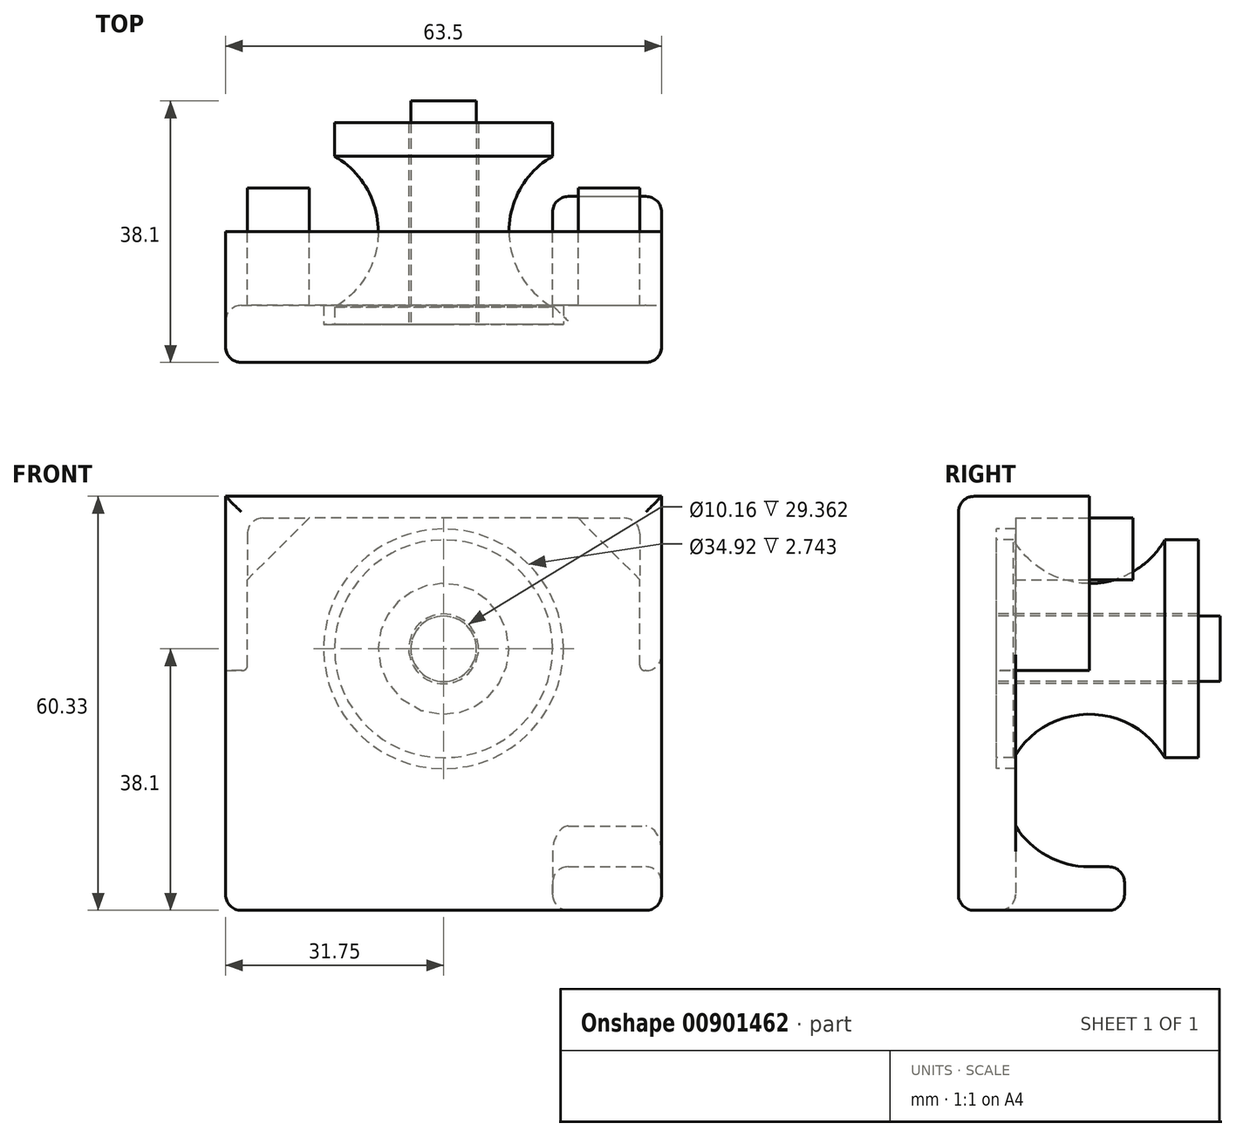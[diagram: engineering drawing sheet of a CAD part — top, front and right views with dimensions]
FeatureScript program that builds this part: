
annotation { "Feature Type Name" : "Feature", "Feature Type Description" : "" }
export const myFeature = defineFeature(function(context is Context, id is Id, definition is map)
    precondition{}
    {
        {
            var Q0;
            Q0=qCreatedBy(makeId("Right.planeOp"),FACE);
            var sketch = newSketch(context, id + "F0", { "sketchPlane" : qUnion([Q0])});
            skLineSegment(sketch, "E0", {"start": v(-15.88, 0) * mm, "end": v(15.88, 0) * mm});
            skLineSegment(sketch, "E1", {"start": v(-15.88, 0) * mm, "end": v(-15.88, 15.88) * mm});
            skArc(sketch, "E2", {"start": v(-11, 15.88) * mm, "mid": v(-6.35, 11.23) * mm, "end": v(0, 9.53) * mm});
            skLineSegment(sketch, "E3", {"start": v(-15.88, 15.88) * mm, "end": v(-11, 15.88) * mm});
            skLineSegment(sketch, "E4", {"start": v(0, 9.53) * mm, "end": v(0, 0) * mm, "construction": true});
            skArc(sketch, "E5.MirrorCS", {"start": v(11, 15.87) * mm, "mid": v(6.35, 11.23) * mm, "end": v(0, 9.53) * mm});
            skLineSegment(sketch, "E6.MirrorCS", {"start": v(15.88, 15.87) * mm, "end": v(11, 15.87) * mm});
            skLineSegment(sketch, "E7.MirrorCS", {"start": v(15.87, 0) * mm, "end": v(15.88, 15.87) * mm});
            skPoint(sketch, "E8.orphan", {"position": v(-16.53, 0) * mm});
            skSolve(sketch);
        }
        {
            var Q0;
            Q0=qSketchRegion(id+"F0",true);
            var Q1;
            Q1=sQuery(id+"F0.wireOp",EDGE,"E0");
            revolve(context, id + "F1", {"surfaceOperationType" : NewSurfaceOperationType.NEW, "entities" : qUnion([Q0]), "axis" : qUnion([Q1]), "revolveType" : RevolveType.FULL});
        }
        {
            var Q0;
            Q0=makeQuery(id+"F1.opRevolve","SWEPT_FACE",FACE,{"disambiguationData":[OSD([sQuery(id+"F0.wireOp",EDGE,"E1")])]});
            cPlane(context, id + "F2", {"entities" : qUnion([Q0]), "cplaneType" : CPlaneType.OFFSET, "offset" : 0.5 * mm, "width" : 152.4 * mm, "height" : 152.4 * mm});
        }
        {
            var Q0;
            Q0=qCreatedBy(id+"F2.planeOp",FACE);
            var sketch = newSketch(context, id + "F3", { "sketchPlane" : qUnion([Q0])});
            skCircle(sketch, "E9", {"center": v(0, 0) * mm, "radius": 5.08 * mm});
            skSolve(sketch);
        }
        {
            var Q0;
            Q0=qSketchRegion(id+"F3",true);
            extrude(context, id + "F4", {"entities" : qUnion([Q0]), "operationType" : NewBodyOperationType.REMOVE, "endBound" : BoundingType.THROUGH_ALL, "oppositeDirection" : true, "depth" : 25.4 * mm, "offsetDistance" : 25.4 * mm});
        }
        {
            var Q0;
            Q0=makeQuery(id+"F1.opRevolve","SWEPT_FACE",FACE,{"disambiguationData":[OSD([sQuery(id+"F0.wireOp",EDGE,"E1")])]});
            var sketch = newSketch(context, id + "F5", { "sketchPlane" : qUnion([Q0])});
            skCircle(sketch, "E10", {"center": v(0, 0) * mm, "radius": 17.46 * mm});
            skLineSegment(sketch, "E11.bottom", {"start": v(-31.75, 38.1) * mm, "end": v(31.75, 38.1) * mm});
            skLineSegment(sketch, "E11.top", {"start": v(-31.75, -38.1) * mm, "end": v(31.75, -38.1) * mm});
            skLineSegment(sketch, "E11.left", {"start": v(-31.75, 38.1) * mm, "end": v(-31.75, -38.1) * mm});
            skLineSegment(sketch, "E11.right", {"start": v(31.75, 38.1) * mm, "end": v(31.75, -38.1) * mm});
            skLineSegment(sketch, "E12", {"start": v(-31.75, 0) * mm, "end": v(31.75, 0) * mm, "construction": true});
            skLineSegment(sketch, "E13", {"start": v(0, 38.1) * mm, "end": v(0, -38.1) * mm, "construction": true});
            skSolve(sketch);
        }
        {
            var Q0;
            Q0=qSketchRegion(id+"F5",true);
            extrude(context, id + "F6", {"entities" : qUnion([Q0]), "oppositeDirection" : true, "depth" : 5.13 * mm, "offsetDistance" : 25.4 * mm, "hasSecondDirection" : true, "secondDirectionOppositeDirection" : false, "secondDirectionDepth" : 3.17 * mm});
        }
        {
            var Q0;
            Q0=makeQuery(id+"F6.opExtrude","CAP_FACE",FACE,{"disambiguationData":[OSD([sQuery(id+"F5.wireOp",EDGE,"E10"),sQuery(id+"F5.wireOp",EDGE,"E11.bottom"),sQuery(id+"F5.wireOp",EDGE,"E11.top"),sQuery(id+"F5.wireOp",EDGE,"E11.left"),sQuery(id+"F5.wireOp",EDGE,"E11.right")])],"isStart":true});
            var sketch = newSketch(context, id + "F7", { "sketchPlane" : qUnion([Q0])});
            skCircle(sketch, "E14.0", {"center": v(0, 0) * mm, "radius": 17.46 * mm});
            skSolve(sketch);
        }
        {
            var Q0;
            Q0=qSketchRegion(id+"F7",true);
            extrude(context, id + "F8", {"entities" : qUnion([Q0]), "operationType" : NewBodyOperationType.ADD, "oppositeDirection" : true, "depth" : 5.56 * mm, "offsetDistance" : 25.4 * mm});
        }
        {
            var Q0;
            Q0=makeQuery(id+"F6.opExtrude","SWEPT_FACE",FACE,{"disambiguationData":[OSD([sQuery(id+"F5.wireOp",EDGE,"E11.right")])]});
            var sketch = newSketch(context, id + "F9", { "sketchPlane" : qUnion([Q0])});
            skArc(sketch, "E15", {"start": v(-10.74, -25.82) * mm, "mid": v(-6.14, -30.17) * mm, "end": v(0, -31.75) * mm});
            skLineSegment(sketch, "E16", {"start": v(-10.74, -25.82) * mm, "end": v(-10.74, -38.1) * mm});
            skLineSegment(sketch, "E17", {"start": v(-10.74, -38.1) * mm, "end": v(0, -38.1) * mm});
            skLineSegment(sketch, "E18", {"start": v(5.13, -38.1) * mm, "end": v(5.13, -31.75) * mm});
            skLineSegment(sketch, "E19", {"start": v(0, -31.75) * mm, "end": v(5.13, -31.75) * mm});
            skLineSegment(sketch, "E20", {"start": v(0, -38.1) * mm, "end": v(5.13, -38.1) * mm});
            skSolve(sketch);
        }
        {
            var Q0;
            Q0=qSketchRegion(id+"F9",true);
            extrude(context, id + "F10", {"entities" : qUnion([Q0]), "operationType" : NewBodyOperationType.ADD, "oppositeDirection" : true, "depth" : 15.88 * mm, "offsetDistance" : 25.4 * mm});
        }
        {
            var Q0;
            Q0=makeQuery(id+"F8.opExtrude","CAP_FACE",FACE,{"disambiguationData":[OSD([sQuery(id+"F7.wireOp",EDGE,"E14.0")])],"isStart":false});
            var sketch = newSketch(context, id + "F11", { "sketchPlane" : qUnion([Q0])});
            skCircle(sketch, "E21", {"center": v(0, 0) * mm, "radius": 4.76 * mm});
            skSolve(sketch);
        }
        {
            var Q0;
            Q0=qSketchRegion(id+"F11",true);
            extrude(context, id + "F12", {"entities" : qUnion([Q0]), "operationType" : NewBodyOperationType.ADD, "depth" : 32.54 * mm, "offsetDistance" : 25.4 * mm});
        }
        {
            var Q0;
            Q0=makeQuery(id+"F6.opExtrude","CAP_FACE",FACE,{"disambiguationData":[OSD([sQuery(id+"F5.wireOp",EDGE,"E10"),sQuery(id+"F5.wireOp",EDGE,"E11.bottom"),sQuery(id+"F5.wireOp",EDGE,"E11.top"),sQuery(id+"F5.wireOp",EDGE,"E11.left"),sQuery(id+"F5.wireOp",EDGE,"E11.right")])],"isStart":false});
            var sketch = newSketch(context, id + "F13", { "sketchPlane" : qUnion([Q0])});
            skLineSegment(sketch, "E22.bottom", {"start": v(-31.75, 22.23) * mm, "end": v(31.75, 22.23) * mm});
            skLineSegment(sketch, "E22.top", {"start": v(-28.58, 19.05) * mm, "end": v(28.57, 19.05) * mm});
            skLineSegment(sketch, "E22.left", {"start": v(-31.75, 22.23) * mm, "end": v(-31.75, 19.05) * mm});
            skLineSegment(sketch, "E22.right", {"start": v(31.75, 22.23) * mm, "end": v(31.75, -3.17) * mm});
            skLineSegment(sketch, "E23", {"start": v(-31.75, 19.05) * mm, "end": v(-31.75, -3.18) * mm});
            skLineSegment(sketch, "E24", {"start": v(-31.75, -3.18) * mm, "end": v(-28.57, -3.18) * mm});
            skLineSegment(sketch, "E25", {"start": v(-28.57, -3.18) * mm, "end": v(-28.57, 19.05) * mm});
            skLineSegment(sketch, "E26", {"start": v(31.75, -3.17) * mm, "end": v(28.57, -3.17) * mm});
            skLineSegment(sketch, "E27", {"start": v(28.57, -3.17) * mm, "end": v(28.57, 19.05) * mm});
            skPoint(sketch, "E28.orphan", {"position": v(31.75, 19.05) * mm});
            skPoint(sketch, "E29.orphan", {"position": v(-31.75, 0) * mm});
            skSolve(sketch);
        }
        {
            var Q0;
            Q0=qSketchRegion(id+"F13",true);
            var Q1;
            Q1=qCreatedBy(makeId("Front.planeOp"),FACE);
            extrude(context, id + "F14", {"entities" : qUnion([Q0]), "operationType" : NewBodyOperationType.ADD, "endBound" : BoundingType.UP_TO_SURFACE, "depth" : 25.4 * mm, "endBoundEntityFace" : qUnion([Q1]), "offsetDistance" : 25.4 * mm});
        }
        {
            var Q0;
            {var subQ0=sQuery(id+"F5.wireOp",EDGE,"E11.right");var subQ1=sQuery(id+"F5.wireOp",EDGE,"E11.left");var subQ2=sQuery(id+"F5.wireOp",EDGE,"E11.bottom");Q0=makeQuery(id+"F14.boolean.opBoolean","SPLIT",FACE,{"disambiguationData":[TD([makeQuery(id+"F6.opExtrude","SWEPT_FACE",FACE,{"disambiguationData":[OSD([subQ2])]})])],"derivedFrom":makeQuery(id+"F6.opExtrude","CAP_FACE",FACE,{"disambiguationData":[OSD([sQuery(id+"F5.wireOp",EDGE,"E10"),subQ2,sQuery(id+"F5.wireOp",EDGE,"E11.top"),subQ1,subQ0])],"isStart":false})});}
            var sketch = newSketch(context, id + "F15", { "sketchPlane" : qUnion([Q0])});
            skCircle(sketch, "E30", {"center": v(-19.05, 30.16) * mm, "radius": 2.4 * mm});
            skCircle(sketch, "E31", {"center": v(19.05, 30.16) * mm, "radius": 2.4 * mm});
            skLineSegment(sketch, "E32", {"start": v(-19.05, 30.16) * mm, "end": v(19.05, 30.16) * mm, "construction": true});
            skSolve(sketch);
        }
        {
            var Q0;
            Q0=qSketchRegion(id+"F15",true);
            extrude(context, id + "F16", {"entities" : qUnion([Q0]), "operationType" : NewBodyOperationType.REMOVE, "endBound" : BoundingType.THROUGH_ALL, "oppositeDirection" : true, "depth" : 25.4 * mm, "offsetDistance" : 25.4 * mm});
        }
        {
            var Q0;
            {var subQ0=sQuery(id+"F5.wireOp",EDGE,"E11.right");var subQ1=sQuery(id+"F5.wireOp",EDGE,"E11.left");var subQ2=sQuery(id+"F5.wireOp",EDGE,"E11.bottom");Q0=makeQuery(id+"F14.boolean.opBoolean","SPLIT",FACE,{"disambiguationData":[TD([makeQuery(id+"F6.opExtrude","SWEPT_FACE",FACE,{"disambiguationData":[OSD([subQ2])]})])],"derivedFrom":makeQuery(id+"F6.opExtrude","CAP_FACE",FACE,{"disambiguationData":[OSD([sQuery(id+"F5.wireOp",EDGE,"E10"),subQ2,sQuery(id+"F5.wireOp",EDGE,"E11.top"),subQ1,subQ0])],"isStart":false})});}
            var sketch = newSketch(context, id + "F17", { "sketchPlane" : qUnion([Q0])});
            skLineSegment(sketch, "E33.0", {"start": v(31.75, 38.1) * mm, "end": v(-31.75, 38.1) * mm});
            skLineSegment(sketch, "E33.1", {"start": v(-31.75, 22.23) * mm, "end": v(31.75, 22.23) * mm});
            skLineSegment(sketch, "E33.2", {"start": v(-31.75, 38.1) * mm, "end": v(-31.75, 22.23) * mm});
            skLineSegment(sketch, "E33.3", {"start": v(31.75, 38.1) * mm, "end": v(31.75, 22.23) * mm});
            skPoint(sketch, "E33.4", {"position": v(-31.75, 30.16) * mm});
            skSolve(sketch);
        }
        {
            var Q0;
            Q0 = qSketchRegion(id + "F17", true);
            extrude(context, id + "F18", {"entities" : qUnion([Q0]), "operationType" : NewBodyOperationType.REMOVE, "oppositeDirection" : true, "depth" : 25.4 * mm, "offsetDistance" : 25.4 * mm});
        }
        {
            var Q0;
            Q0=makeQuery(id+"F14.opExtrude","SWEPT_EDGE",EDGE,{"disambiguationData":[OSD([sQuery(id+"F13.wireOp",EDGE,"E22.top"),sQuery(id+"F13.wireOp",EDGE,"E25")])]});
            var Q1;
            Q1=makeQuery(id+"F14.opExtrude","SWEPT_EDGE",EDGE,{"disambiguationData":[OSD([sQuery(id+"F13.wireOp",EDGE,"E22.top"),sQuery(id+"F13.wireOp",EDGE,"E27")])]});
            var Q2;
            Q2=makeQuery(id+"F10.opExtrude","CAP_EDGE",EDGE,{"disambiguationData":[OSD([sQuery(id+"F9.wireOp",EDGE,"E15")])],"isStart":true});
            var Q3;
            Q3=makeQuery(id+"F10.opExtrude","CAP_EDGE",EDGE,{"disambiguationData":[OSD([sQuery(id+"F9.wireOp",EDGE,"E15")])],"isStart":false});
            var Q4;
            Q4=makeQuery(id+"F10.opExtrude","SWEPT_FACE",FACE,{"disambiguationData":[OSD([sQuery(id+"F9.wireOp",EDGE,"E18")])]});
            var Q5;
            Q5=makeQuery(id+"F10.boolean.opBoolean","MERGE",EDGE,{"derivedFrom":[makeQuery(id+"F6.opExtrude","SWEPT_EDGE",EDGE,{"disambiguationData":[OSD([sQuery(id+"F5.wireOp",EDGE,"E11.top"),sQuery(id+"F5.wireOp",EDGE,"E11.right")])]}),makeQuery(id+"F10.opExtrude","CAP_EDGE",EDGE,{"disambiguationData":[OSD([sQuery(id+"F9.wireOp",EDGE,"E17"),sQuery(id+"F9.wireOp",EDGE,"E20")])],"isStart":true})]});
            var Q6;
            Q6=makeQuery(id+"F10.opExtrude","CAP_EDGE",EDGE,{"disambiguationData":[OSD([sQuery(id+"F9.wireOp",EDGE,"E17"),sQuery(id+"F9.wireOp",EDGE,"E20")])],"isStart":false});
            var Q7;
            Q7=makeQuery(id+"F6.opExtrude","CAP_EDGE",EDGE,{"disambiguationData":[OSD([sQuery(id+"F5.wireOp",EDGE,"E11.top")])],"isStart":false});
            var Q8;
            Q8=makeQuery(id+"F6.opExtrude","CAP_EDGE",EDGE,{"disambiguationData":[OSD([sQuery(id+"F5.wireOp",EDGE,"E11.top")])],"isStart":true});
            var Q9;
            Q9=makeQuery(id+"F6.opExtrude","SWEPT_FACE",FACE,{"disambiguationData":[OSD([sQuery(id+"F5.wireOp",EDGE,"E11.bottom")])]});
            var Q10;
            Q10=makeQuery(id+"F14.opExtrude","CAP_EDGE",EDGE,{"disambiguationData":[OSD([sQuery(id+"F13.wireOp",EDGE,"E22.bottom")])],"isStart":true});
            var Q11;
            Q11=makeQuery(id+"F14.opExtrude","CAP_EDGE",EDGE,{"disambiguationData":[OSD([sQuery(id+"F13.wireOp",EDGE,"E22.top")])],"isStart":true});
            var Q12;
            Q12=makeQuery(id+"F14.opExtrude","CAP_EDGE",EDGE,{"disambiguationData":[OSD([sQuery(id+"F13.wireOp",EDGE,"E25")])],"isStart":true});
            var Q13;
            Q13=makeQuery(id+"F14.opExtrude","CAP_EDGE",EDGE,{"disambiguationData":[OSD([sQuery(id+"F13.wireOp",EDGE,"E27")])],"isStart":true});
            var Q14;
            Q14=makeQuery(id+"F14.opExtrude","CAP_EDGE",EDGE,{"disambiguationData":[OSD([sQuery(id+"F13.wireOp",EDGE,"E26")])],"isStart":true});
            var Q15;
            {var subQ0=sQuery(id+"F5.wireOp",EDGE,"E11.left");var subQ1=sQuery(id+"F5.wireOp",EDGE,"E11.top");Q15=makeQuery(id+"F14.boolean.opBoolean","SPLIT",EDGE,{"disambiguationData":[TD([makeQuery(id+"F6.opExtrude","SWEPT_FACE",FACE,{"disambiguationData":[OSD([subQ1])]})])],"derivedFrom":makeQuery(id+"F6.opExtrude","CAP_EDGE",EDGE,{"disambiguationData":[OSD([subQ0])],"isStart":false})});}
            var Q16;
            Q16=makeQuery(id+"F6.opExtrude","SWEPT_EDGE",EDGE,{"disambiguationData":[OSD([sQuery(id+"F5.wireOp",EDGE,"E11.top"),sQuery(id+"F5.wireOp",EDGE,"E11.left")])]});
            var Q17;
            Q17=makeQuery(id+"F6.opExtrude","CAP_EDGE",EDGE,{"disambiguationData":[OSD([sQuery(id+"F5.wireOp",EDGE,"E11.left")])],"isStart":true});
            var Q18;
            Q18=makeQuery(id+"F14.opExtrude","SWEPT_EDGE",EDGE,{"disambiguationData":[OSD([sQuery(id+"F5.wireOp",EDGE,"E11.left"),sQuery(id+"F13.wireOp",EDGE,"E22.bottom"),sQuery(id+"F13.wireOp",EDGE,"E22.right")])]});
            var Q19;
            Q19=makeQuery(id+"F14.opExtrude","CAP_EDGE",EDGE,{"disambiguationData":[OSD([sQuery(id+"F13.wireOp",EDGE,"E24")])],"isStart":true});
            var Q20;
            Q20=makeQuery(id+"F14.opExtrude","SWEPT_EDGE",EDGE,{"disambiguationData":[OSD([sQuery(id+"F5.wireOp",EDGE,"E11.right"),sQuery(id+"F13.wireOp",EDGE,"E23"),sQuery(id+"F13.wireOp",EDGE,"E24")])]});
            var Q21;
            Q21=makeQuery(id+"F14.opExtrude","SWEPT_EDGE",EDGE,{"disambiguationData":[OSD([sQuery(id+"F5.wireOp",EDGE,"E11.right"),sQuery(id+"F13.wireOp",EDGE,"E22.bottom"),sQuery(id+"F13.wireOp",EDGE,"E22.left")])]});
            var Q22;
            Q22=makeQuery(id+"F6.opExtrude","CAP_EDGE",EDGE,{"disambiguationData":[OSD([sQuery(id+"F5.wireOp",EDGE,"E11.right")])],"isStart":true});
            var Q23;
            Q23=makeQuery(id+"F18.boolean.opBoolean","INTERSECT",EDGE,{"derivedFrom":[makeQuery(id+"F8.boolean.opBoolean","MERGE",FACE,{"derivedFrom":[makeQuery(id+"F6.opExtrude","CAP_FACE",FACE,{"disambiguationData":[OSD([sQuery(id+"F5.wireOp",EDGE,"E10"),sQuery(id+"F5.wireOp",EDGE,"E11.bottom"),sQuery(id+"F5.wireOp",EDGE,"E11.top"),sQuery(id+"F5.wireOp",EDGE,"E11.left"),sQuery(id+"F5.wireOp",EDGE,"E11.right")])],"isStart":true}),makeQuery(id+"F8.opExtrude","CAP_FACE",FACE,{"disambiguationData":[OSD([sQuery(id+"F7.wireOp",EDGE,"E14.0")])],"isStart":true})]}),makeQuery(id+"F18.opExtrude","SWEPT_FACE",FACE,{"disambiguationData":[OSD([sQuery(id+"F17.wireOp",EDGE,"E33.1")])]})]});
            fillet(context, id + "F19", {"entities" : qUnion([Q0, Q1, Q2, Q3, Q4, Q5, Q6, Q7, Q8, Q9, Q10, Q11, Q12, Q13, Q14, Q15, Q16, Q17, Q18, Q19, Q20, Q21, Q22, Q23]), "radius" : 2.3 * mm, "tangentPropagation" : true, "allowEdgeOverflow" : false});
        }
        {
            var Q0;
            Q0=makeQuery(id+"F14.opExtrude","SWEPT_EDGE",EDGE,{"disambiguationData":[OSD([sQuery(id+"F13.wireOp",EDGE,"E24"),sQuery(id+"F13.wireOp",EDGE,"E25")])]});
            var Q1;
            Q1=makeQuery(id+"F14.opExtrude","SWEPT_EDGE",EDGE,{"disambiguationData":[OSD([sQuery(id+"F13.wireOp",EDGE,"E26"),sQuery(id+"F13.wireOp",EDGE,"E27")])]});
            fillet(context, id + "F20", {"entities" : qUnion([Q0, Q1]), "radius" : 0.76 * mm, "tangentPropagation" : true, "allowEdgeOverflow" : false});
        }
        {
            var Q0;
            Q0=qCreatedBy(makeId("Front.planeOp"),FACE);
            var sketch = newSketch(context, id + "F21", { "sketchPlane" : qUnion([Q0])});
            skLineSegment(sketch, "E34.0", {"start": v(28.57, 16.76) * mm, "end": v(28.57, 10.07) * mm});
            skArc(sketch, "E34.1", {"start": v(28.57, 16.76) * mm, "mid": v(27.9, 18.38) * mm, "end": v(26.29, 19.05) * mm});
            skLineSegment(sketch, "E34.2", {"start": v(-26.29, 19.05) * mm, "end": v(-19.6, 19.05) * mm});
            skArc(sketch, "E34.3", {"start": v(-26.29, 19.05) * mm, "mid": v(-27.9, 18.38) * mm, "end": v(-28.57, 16.76) * mm});
            skLineSegment(sketch, "E34.4", {"start": v(-28.57, 16.76) * mm, "end": v(-28.57, 10.07) * mm});
            skLineSegment(sketch, "E35", {"start": v(19.6, 19.05) * mm, "end": v(28.57, 10.07) * mm});
            skLineSegment(sketch, "E36", {"start": v(-19.6, 19.05) * mm, "end": v(-28.57, 10.07) * mm});
            skLineSegment(sketch, "E37.trimOffspring", {"start": v(19.6, 19.05) * mm, "end": v(26.29, 19.05) * mm});
            skPoint(sketch, "E38.orphan", {"position": v(28.57, -2.41) * mm});
            skPoint(sketch, "E39.orphan", {"position": v(-28.57, -2.41) * mm});
            skSolve(sketch);
        }
        {
            var Q0;
            Q0 = qSketchRegion(id + "F21", true);
            var Q1;
            {var subQ2=sQuery(id+"F5.wireOp",EDGE,"E10");var subQ7=sQuery(id+"F5.wireOp",EDGE,"E11.left");var subQ8=sQuery(id+"F5.wireOp",EDGE,"E11.top");var subQ9=sQuery(id+"F5.wireOp",EDGE,"E11.right");Q1=makeQuery(id+"F14.boolean.opBoolean","SPLIT",FACE,{"disambiguationData":[TD([makeQuery(id+"F6.opExtrude","SWEPT_FACE",FACE,{"disambiguationData":[OSD([subQ2])]})])],"derivedFrom":makeQuery(id+"F6.opExtrude","CAP_FACE",FACE,{"disambiguationData":[OSD([subQ2,sQuery(id+"F5.wireOp",EDGE,"E11.bottom"),subQ8,subQ7,subQ9])],"isStart":false})});}
            extrude(context, id + "F22", {"entities" : qUnion([Q0]), "operationType" : NewBodyOperationType.ADD, "endBound" : BoundingType.UP_TO_SURFACE, "depth" : 25.4 * mm, "endBoundEntityFace" : qUnion([Q1]), "offsetDistance" : 25.4 * mm, "hasSecondDirection" : true, "secondDirectionOppositeDirection" : true, "secondDirectionDepth" : 6.35 * mm});
        }
    });
